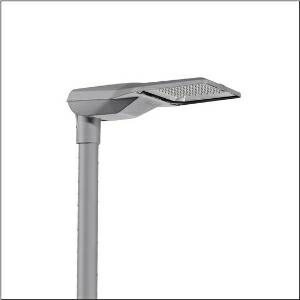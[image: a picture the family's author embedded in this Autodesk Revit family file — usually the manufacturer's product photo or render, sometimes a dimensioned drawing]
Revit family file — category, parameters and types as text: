
# Revit family: streetlight_sl_21_iq_midi___st1_0ab_5xe3m31d08nb_cbc2
name_source: partatom
category: Lighting Fixtures
units: mm (PartAtom-declared; Revit-internal decimal feet)

## family parameters
Cut with Voids When Loaded = No
Host = Face
Light Source = No
Part Type = Normal
Room Calculation Point = No
Round Connector Dimension = Use Diameter
Shared = No

## types (1)
- --- (1 x LED, 20440 lm, 155.5 W, 3000K)
    Apparent Load = 155 VA
    CIE Flux Codes = 40 74 97 100 100
    Color Rendering = 70
    Color Temperature = 3000K
    Default Elevation = 1800 mm
    Description = Streetlight SL 21 iQ midi, mast luminaire, primary light control with lens, of PMMA, primary optical cover: cover, of toughened safety glass, transparent, light distribution: ST1.0aB, light emission: direct distribution, primary light characteristic: asymmetric, installation type: post-top, side-entry, LED, High Power LED, rated luminous flux: 20.440lm, luminous efficacy: 131lm/W, light colour: 730, colour temperature: 3000K, control gear: iQ-Comfort, control: Auto-Match, Temp-Guard, Lumen-Switch, Night-Set, Smart-Wire, Light-Fading, Desk-Remote (wireless, voltage-free reading and setting of iQ features in the workshop via application-optimized NFC function/RFID function), optimised constant luminous flux control (CLO 2.0), pre-setting: linear dimming characteristic, mains connection: 230..240V, AC, 50/60Hz, start of lifetime: 156W, end of service life: 162W, reduction: 69W, luminaire housing, of diecast aluminium, powder-coated, SITECO metallic grey (DB 702S), corrosivity category C5 high according to DIN EN ISO 12944, please order mast flange separately, inclination adjustable: 0°, 5°, 10°, 15°, sealing non-destructively replaceable, multi-level sealing system, length: 644mm, width: 335mm, height: 110mm, mast flange for spigot size: 42mm (side-entry): 5XC10008XM4, 60/48mm (side-entry/post-top): 5XC10108XM2, 76/60mm (side-entry/post-top): 5XC10108XM1, mounting height: 4..8m, protection rating (complete): IP66, insulation class (complete): insulation class II (safety insulation), certification: CE, ENEC, ENEC+, VDE, impact resistance: IK10, permissible operating ambient temperature for outdoor applications: -40..+50°C, standard-compliant lighting for roads and squares, packaging unit: 1 piece

Light Distribution: ST1.0aB
    Height = 111 mm
    Lamp = 1 x LED
    Lamp Light Flux = 20440 lm
    Lamp Power = 155.5 W
    Lamp count = 1
    Length = 644 mm
    Luminous efficacy = 131 lm/W
    Manufacturer = Siteco
    ModVariant = No
    Model = 5XE3M31D08NB
    Number of Poles = 1
    OnlyDefault = Yes
    Power Factor = 1
    Product Name = Streetlight SL 21 iQ midi | ST1.0aB
    Product group = mast luminaire | pylon top
    ProductGroupID = 6100
    Protection Class = Protection class II
    Protection Degree = IP 66
    RLX_Detail_Level = 1
    RLX_Emergency_Light_Flux = 0 lm
    RLX_Emergency_Type = 0
    RLX_Emergency_Type_DB = No
    RlxData = <blob elided: 27201 chars, md5=e0c818cc>
    Socket = socket
    Standby Power = 0 W
    System Light Flux = 20440 lm
    System Power = 155 W
    Type Comments = factory setting: luminous flux: 100 % | dim-lin: 254 | 823 mA
    Type Image = l_1004298.jpg
    URL = http://relux.com
    VarID = @adj_167739
    Voltage = 0 V
    Weight = 0.00 kg
    Width = 336 mm

## geometry (parser evidence)
native form markers: Blend x4, Sweep x11
no freeform markers — native parametric forms only
